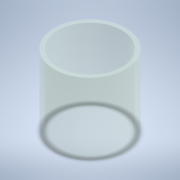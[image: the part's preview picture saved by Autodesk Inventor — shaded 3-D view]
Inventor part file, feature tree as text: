
AUTODESK INVENTOR PART (.ipt)
format: ipt  version: 2020 (Build 240168000, 168)  size: 118,272 bytes
history: native  units: mm
features: other x1, extrude x1, sketch x1
ambient origin geometry x8: Origin, YZ Plane, XZ Plane, XY Plane, X Axis, Y Axis, Z Axis, Center Point
bodies: Body1 (feature_tree)
feature tree (3):
  other  "Твердое тело1"
  extrude  "Выдавливание1"  Depth=50.0mm
  sketch  "Эскиз1"
